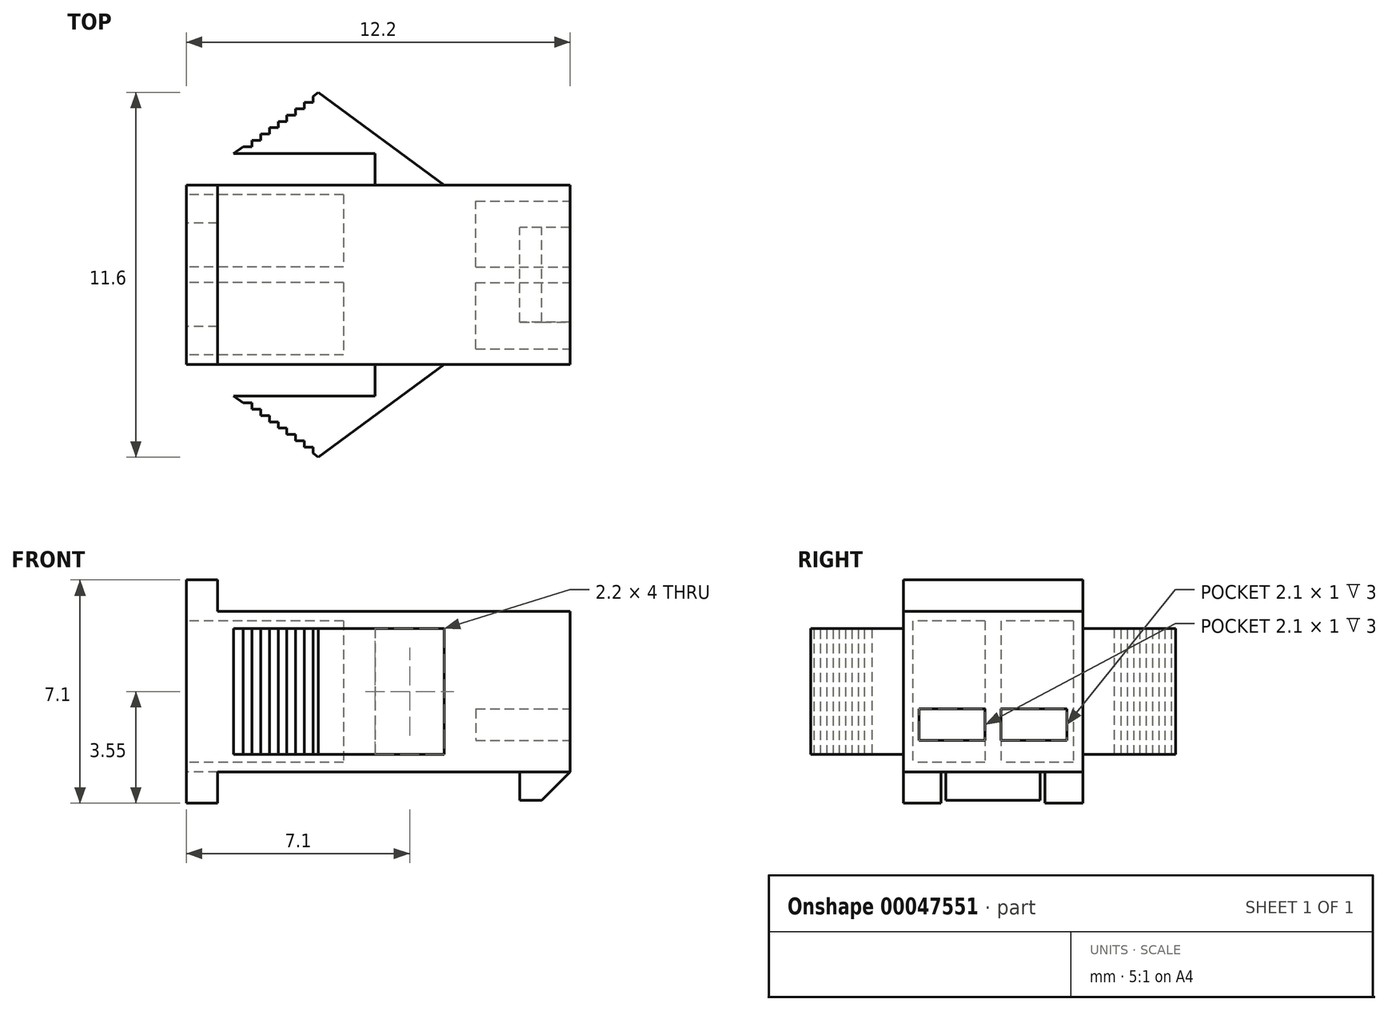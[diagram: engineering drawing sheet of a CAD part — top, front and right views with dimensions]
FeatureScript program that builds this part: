
annotation { "Feature Type Name" : "Feature", "Feature Type Description" : "" }
export const myFeature = defineFeature(function(context is Context, id is Id, definition is map)
    precondition{}
    {
        {
            var Q0;
            Q0=qCreatedBy(makeId("Top.planeOp"),FACE);
            var sketch = newSketch(context, id + "F0", { "sketchPlane" : qUnion([Q0])});
            skLineSegment(sketch, "E0.bottom", {"start": v(-6.1, 2.85) * mm, "end": v(-0.1, 2.85) * mm});
            skLineSegment(sketch, "E0.top", {"start": v(-6.1, -2.85) * mm, "end": v(-0.1, -2.85) * mm});
            skLineSegment(sketch, "E0.left", {"start": v(-6.1, 2.85) * mm, "end": v(-6.1, -2.85) * mm});
            skLineSegment(sketch, "E0.right", {"start": v(6.1, 2.85) * mm, "end": v(6.1, -2.85) * mm});
            skLineSegment(sketch, "E1", {"start": v(2.1, 2.85) * mm, "end": v(-1.9, 5.8) * mm});
            skLineSegment(sketch, "E2", {"start": v(2.1, -2.85) * mm, "end": v(-1.9, -5.8) * mm});
            skLineSegment(sketch, "E3", {"start": v(-4.6, 3.85) * mm, "end": v(-0.1, 3.85) * mm});
            skLineSegment(sketch, "E4", {"start": v(-1.9, 5.8) * mm, "end": v(-4.6, 3.85) * mm});
            skLineSegment(sketch, "E5.trimOffspring", {"start": v(-0.1, 3.85) * mm, "end": v(-0.1, 2.85) * mm});
            skLineSegment(sketch, "E6.trimOffspring", {"start": v(-0.1, -2.85) * mm, "end": v(-0.1, -3.85) * mm});
            skLineSegment(sketch, "E7", {"start": v(-4.6, -3.85) * mm, "end": v(-0.1, -3.85) * mm});
            skLineSegment(sketch, "E8", {"start": v(-4.6, -3.85) * mm, "end": v(-1.9, -5.8) * mm});
            skLineSegment(sketch, "E9.trimOffspring", {"start": v(2.1, 2.85) * mm, "end": v(6.1, 2.85) * mm});
            skLineSegment(sketch, "E10.trimOffspring", {"start": v(2.1, -2.85) * mm, "end": v(6.1, -2.85) * mm});
            skSolve(sketch);
        }
        {
            var Q0;
            Q0 = qSketchRegion(id + "F0", true);
            extrude(context, id + "F1", {"entities" : qUnion([Q0]), "depth" : 5.1 * mm});
        }
        {
            var Q0;
            Q0=makeQuery(id+"F1.opExtrude","SWEPT_FACE",FACE,{"disambiguationData":[OSD([sQuery(id+"F0.wireOp",EDGE,"E0.right")])]});
            var sketch = newSketch(context, id + "F2", { "sketchPlane" : qUnion([Q0])});
            skLineSegment(sketch, "E11", {"start": v(-6.2, 5.1) * mm, "end": v(-6.2, 4.55) * mm});
            skLineSegment(sketch, "E12", {"start": v(-6.2, 4.55) * mm, "end": v(-2.85, 4.55) * mm});
            skLineSegment(sketch, "E13", {"start": v(-6.2, 0.55) * mm, "end": v(-2.85, 0.55) * mm});
            skLineSegment(sketch, "E14", {"start": v(6.15, 5.1) * mm, "end": v(6.15, 4.55) * mm});
            skLineSegment(sketch, "E15", {"start": v(-2.85, 4.55) * mm, "end": v(-2.85, 5.1) * mm});
            skLineSegment(sketch, "E16", {"start": v(-2.85, 5.1) * mm, "end": v(-6.2, 5.1) * mm});
            skLineSegment(sketch, "E17", {"start": v(-2.85, 0.55) * mm, "end": v(-2.85, 0) * mm});
            skLineSegment(sketch, "E18", {"start": v(-2.85, 0) * mm, "end": v(-6.2, 0) * mm});
            skLineSegment(sketch, "E19", {"start": v(2.85, 4.55) * mm, "end": v(2.85, 5.1) * mm});
            skLineSegment(sketch, "E20", {"start": v(2.85, 5.1) * mm, "end": v(6.15, 5.1) * mm});
            skLineSegment(sketch, "E21", {"start": v(2.85, 0.55) * mm, "end": v(2.85, 0) * mm});
            skLineSegment(sketch, "E22", {"start": v(2.85, 0) * mm, "end": v(6.15, 0) * mm});
            skLineSegment(sketch, "E23.trimOffspring", {"start": v(6.15, 0.55) * mm, "end": v(6.15, 0) * mm});
            skLineSegment(sketch, "E24.trimOffspring", {"start": v(-6.2, 0.55) * mm, "end": v(-6.2, 0) * mm});
            skLineSegment(sketch, "E25.trimOffspring", {"start": v(2.85, 4.55) * mm, "end": v(6.15, 4.55) * mm});
            skLineSegment(sketch, "E26.trimOffspring", {"start": v(2.85, 0.55) * mm, "end": v(6.15, 0.55) * mm});
            skSolve(sketch);
        }
        {
            var Q0;
            Q0 = qSketchRegion(id + "F2", true);
            extrude(context, id + "F3", {"entities" : qUnion([Q0]), "operationType" : NewBodyOperationType.REMOVE, "oppositeDirection" : true, "depth" : 15 * mm});
        }
        {
            var Q0;
            Q0=makeQuery(id+"F3.boolean.opBoolean","COPY",FACE,{"derivedFrom":makeQuery(id+"F3.opExtrude","SWEPT_FACE",FACE,{"disambiguationData":[OSD([sQuery(id+"F2.wireOp",EDGE,"E25.trimOffspring")])]})});
            var sketch = newSketch(context, id + "F4", { "sketchPlane" : qUnion([Q0])});
            skLineSegment(sketch, "E27.0", {"start": v(-2.07, 5.48) * mm, "end": v(-2.35, 5.48) * mm});
            skLineSegment(sketch, "E28.0", {"start": v(-2.35, 5.28) * mm, "end": v(-2.63, 5.28) * mm});
            skLineSegment(sketch, "E29.0", {"start": v(-2.63, 5.08) * mm, "end": v(-2.9, 5.08) * mm});
            skLineSegment(sketch, "E30.0", {"start": v(-2.9, 4.88) * mm, "end": v(-3.18, 4.88) * mm});
            skLineSegment(sketch, "E31.0", {"start": v(-3.18, 4.68) * mm, "end": v(-3.46, 4.68) * mm});
            skLineSegment(sketch, "E32.0", {"start": v(-3.46, 4.48) * mm, "end": v(-3.73, 4.48) * mm});
            skLineSegment(sketch, "E33.0", {"start": v(-3.73, 4.28) * mm, "end": v(-4.01, 4.28) * mm});
            skLineSegment(sketch, "E34", {"start": v(-2.07, 5.68) * mm, "end": v(-2.07, 5.48) * mm});
            skLineSegment(sketch, "E35", {"start": v(-2.35, 5.48) * mm, "end": v(-2.35, 5.28) * mm});
            skLineSegment(sketch, "E36", {"start": v(-2.63, 5.28) * mm, "end": v(-2.63, 5.08) * mm});
            skLineSegment(sketch, "E37", {"start": v(-2.9, 5.08) * mm, "end": v(-2.9, 4.88) * mm});
            skLineSegment(sketch, "E38", {"start": v(-3.18, 4.88) * mm, "end": v(-3.18, 4.68) * mm});
            skLineSegment(sketch, "E39", {"start": v(-3.46, 4.68) * mm, "end": v(-3.46, 4.48) * mm});
            skLineSegment(sketch, "E40", {"start": v(-3.73, 4.48) * mm, "end": v(-3.73, 4.28) * mm});
            skLineSegment(sketch, "E41.0", {"start": v(-4.01, 4.08) * mm, "end": v(-4.29, 4.08) * mm});
            skLineSegment(sketch, "E42", {"start": v(-4.01, 4.28) * mm, "end": v(-4.01, 4.08) * mm});
            skLineSegment(sketch, "E43", {"start": v(-2.07, 5.68) * mm, "end": v(-4.29, 4.08) * mm});
            skLineSegment(sketch, "E44.MirrorCS", {"start": v(-3.46, -4.68) * mm, "end": v(-3.46, -4.48) * mm});
            skLineSegment(sketch, "E45.MirrorCS", {"start": v(-3.18, -4.88) * mm, "end": v(-3.18, -4.68) * mm});
            skLineSegment(sketch, "E46.MirrorCS", {"start": v(-3.18, -4.68) * mm, "end": v(-3.46, -4.68) * mm});
            skLineSegment(sketch, "E47.MirrorCS", {"start": v(-2.9, -5.08) * mm, "end": v(-2.9, -4.88) * mm});
            skLineSegment(sketch, "E48.MirrorCS", {"start": v(-2.63, -5.28) * mm, "end": v(-2.63, -5.08) * mm});
            skLineSegment(sketch, "E49.MirrorCS", {"start": v(-2.35, -5.48) * mm, "end": v(-2.35, -5.28) * mm});
            skLineSegment(sketch, "E50.MirrorCS", {"start": v(-2.07, -5.68) * mm, "end": v(-2.07, -5.48) * mm});
            skLineSegment(sketch, "E51.MirrorCS", {"start": v(-3.73, -4.28) * mm, "end": v(-4.01, -4.28) * mm});
            skLineSegment(sketch, "E52.MirrorCS", {"start": v(-3.46, -4.48) * mm, "end": v(-3.73, -4.48) * mm});
            skLineSegment(sketch, "E53.MirrorCS", {"start": v(-2.9, -4.88) * mm, "end": v(-3.18, -4.88) * mm});
            skLineSegment(sketch, "E54.MirrorCS", {"start": v(-2.63, -5.08) * mm, "end": v(-2.9, -5.08) * mm});
            skLineSegment(sketch, "E55.MirrorCS", {"start": v(-2.35, -5.28) * mm, "end": v(-2.63, -5.28) * mm});
            skLineSegment(sketch, "E56.MirrorCS", {"start": v(-2.07, -5.48) * mm, "end": v(-2.35, -5.48) * mm});
            skLineSegment(sketch, "E57.MirrorCS", {"start": v(-4.01, -4.28) * mm, "end": v(-4.01, -4.08) * mm});
            skLineSegment(sketch, "E58.MirrorCS", {"start": v(-4.01, -4.08) * mm, "end": v(-4.29, -4.08) * mm});
            skLineSegment(sketch, "E59.MirrorCS", {"start": v(-3.73, -4.48) * mm, "end": v(-3.73, -4.28) * mm});
            skLineSegment(sketch, "E60.MirrorCS", {"start": v(-2.07, -5.68) * mm, "end": v(-4.29, -4.08) * mm});
            skSolve(sketch);
        }
        {
            var Q0;
            Q0 = qSketchRegion(id + "F4", true);
            extrude(context, id + "F5", {"entities" : qUnion([Q0]), "operationType" : NewBodyOperationType.REMOVE, "oppositeDirection" : true, "depth" : 25 * mm});
        }
        {
            var Q0;
            Q0 = qSketchRegion(id + "F4", true);
            extrude(context, id + "F6", {"entities" : qUnion([Q0]), "operationType" : NewBodyOperationType.REMOVE, "oppositeDirection" : true, "depth" : 10 * mm});
        }
        {
            var Q0;
            Q0=makeQuery(id+"F1.opExtrude","SWEPT_FACE",FACE,{"disambiguationData":[OSD([sQuery(id+"F0.wireOp",EDGE,"E0.left")])]});
            var sketch = newSketch(context, id + "F7", { "sketchPlane" : qUnion([Q0])});
            skLineSegment(sketch, "E61", {"start": v(-2.85, 5.1) * mm, "end": v(-2.85, 6.1) * mm});
            skLineSegment(sketch, "E62", {"start": v(-2.85, 6.1) * mm, "end": v(2.85, 6.1) * mm});
            skLineSegment(sketch, "E63", {"start": v(2.85, 5.1) * mm, "end": v(2.85, 6.1) * mm});
            skPoint(sketch, "E63.endSnap0", {"position": v(0.35, 6.1) * mm});
            skLineSegment(sketch, "E64", {"start": v(-2.85, 5.1) * mm, "end": v(2.85, 5.1) * mm});
            skLineSegment(sketch, "E65", {"start": v(-2.85, 0) * mm, "end": v(-1.65, 0) * mm});
            skLineSegment(sketch, "E66", {"start": v(2.85, 0) * mm, "end": v(2.85, -1) * mm});
            skLineSegment(sketch, "E67", {"start": v(2.85, -1) * mm, "end": v(1.65, -1) * mm});
            skLineSegment(sketch, "E68", {"start": v(-2.85, -1) * mm, "end": v(-2.85, 0) * mm});
            skLineSegment(sketch, "E69", {"start": v(1.65, 0) * mm, "end": v(1.65, -1) * mm});
            skLineSegment(sketch, "E70", {"start": v(-1.65, 0) * mm, "end": v(-1.65, -1) * mm});
            skLineSegment(sketch, "E71.trimOffspring", {"start": v(-1.65, -1) * mm, "end": v(-2.85, -1) * mm});
            skLineSegment(sketch, "E72.trimOffspring", {"start": v(1.65, 0) * mm, "end": v(2.85, 0) * mm});
            skSolve(sketch);
        }
        {
            var Q0;
            Q0 = qSketchRegion(id + "F7", true);
            extrude(context, id + "F8", {"entities" : qUnion([Q0]), "oppositeDirection" : true, "depth" : 1 * mm});
        }
        {
            var Q0;
            Q0=makeQuery(id+"F1.opExtrude","SWEPT_BODY",BODY,{"disambiguationData":[OSD([sQuery(id+"F0.wireOp",EDGE,"E0.bottom"),sQuery(id+"F0.wireOp",EDGE,"E0.top"),sQuery(id+"F0.wireOp",EDGE,"E0.left"),sQuery(id+"F0.wireOp",EDGE,"E0.right"),sQuery(id+"F0.wireOp",EDGE,"E1"),sQuery(id+"F0.wireOp",EDGE,"E2"),sQuery(id+"F0.wireOp",EDGE,"E3"),sQuery(id+"F0.wireOp",EDGE,"E4"),sQuery(id+"F0.wireOp",EDGE,"E5.trimOffspring"),sQuery(id+"F0.wireOp",EDGE,"E6.trimOffspring"),sQuery(id+"F0.wireOp",EDGE,"E7"),sQuery(id+"F0.wireOp",EDGE,"E8"),sQuery(id+"F0.wireOp",EDGE,"E9.trimOffspring"),sQuery(id+"F0.wireOp",EDGE,"E10.trimOffspring")])]});
            var Q1;
            Q1=makeQuery(id+"F8.opExtrude","SWEPT_BODY",BODY,{"disambiguationData":[OSD([sQuery(id+"F7.wireOp",EDGE,"E65"),sQuery(id+"F7.wireOp",EDGE,"E68"),sQuery(id+"F7.wireOp",EDGE,"E70"),sQuery(id+"F7.wireOp",EDGE,"E71.trimOffspring")])]});
            var Q2;
            Q2=makeQuery(id+"F8.opExtrude","SWEPT_BODY",BODY,{"disambiguationData":[OSD([sQuery(id+"F7.wireOp",EDGE,"E66"),sQuery(id+"F7.wireOp",EDGE,"E67"),sQuery(id+"F7.wireOp",EDGE,"E69"),sQuery(id+"F7.wireOp",EDGE,"E72.trimOffspring")])]});
            var Q3;
            Q3=makeQuery(id+"F8.opExtrude","SWEPT_BODY",BODY,{"disambiguationData":[OSD([sQuery(id+"F7.wireOp",EDGE,"E61"),sQuery(id+"F7.wireOp",EDGE,"E62"),sQuery(id+"F7.wireOp",EDGE,"E63"),sQuery(id+"F7.wireOp",EDGE,"E64")])]});
            booleanBodies(context, id + "F9", {"operationType" : BooleanOperationType.UNION, "tools" : qUnion([Q0, Q1, Q2, Q3])});
        }
        {
            var Q0;
            Q0=makeQuery(id+"F9.opBoolean","MERGE",FACE,{"derivedFrom":[makeQuery(id+"F3.boolean.opBoolean","MERGE",FACE,{"derivedFrom":[makeQuery(id+"F1.opExtrude","SWEPT_FACE",FACE,{"disambiguationData":[OSD([sQuery(id+"F0.wireOp",EDGE,"E0.bottom")])]}),makeQuery(id+"F1.opExtrude","SWEPT_FACE",FACE,{"disambiguationData":[OSD([sQuery(id+"F0.wireOp",EDGE,"E9.trimOffspring")])]}),makeQuery(id+"F3.opExtrude","SWEPT_FACE",FACE,{"disambiguationData":[OSD([sQuery(id+"F2.wireOp",EDGE,"E19")])]}),makeQuery(id+"F3.opExtrude","SWEPT_FACE",FACE,{"disambiguationData":[OSD([sQuery(id+"F2.wireOp",EDGE,"E21")])]})]}),makeQuery(id+"F8.opExtrude","SWEPT_FACE",FACE,{"disambiguationData":[OSD([sQuery(id+"F7.wireOp",EDGE,"E61")])]}),makeQuery(id+"F8.opExtrude","SWEPT_FACE",FACE,{"disambiguationData":[OSD([sQuery(id+"F7.wireOp",EDGE,"E68")])]})]});
            var sketch = newSketch(context, id + "F10", { "sketchPlane" : qUnion([Q0])});
            skLineSegment(sketch, "E73", {"start": v(-5.2, -0.9) * mm, "end": v(-4.5, -0.9) * mm});
            skLineSegment(sketch, "E74", {"start": v(-4.5, -0.9) * mm, "end": v(-4.5, 0) * mm});
            skLineSegment(sketch, "E75", {"start": v(-6.1, 0) * mm, "end": v(-5.2, -0.9) * mm});
            skLineSegment(sketch, "E76", {"start": v(-4.5, 0) * mm, "end": v(-6.1, 0) * mm});
            skSolve(sketch);
        }
        {
            var Q0;
            Q0 = qSketchRegion(id + "F10", true);
            var Q1;
            Q1=makeQuery(id+"F9.opBoolean","MERGE",FACE,{"derivedFrom":[makeQuery(id+"F3.boolean.opBoolean","MERGE",FACE,{"derivedFrom":[makeQuery(id+"F1.opExtrude","SWEPT_FACE",FACE,{"disambiguationData":[OSD([sQuery(id+"F0.wireOp",EDGE,"E0.top")])]}),makeQuery(id+"F1.opExtrude","SWEPT_FACE",FACE,{"disambiguationData":[OSD([sQuery(id+"F0.wireOp",EDGE,"E10.trimOffspring")])]}),makeQuery(id+"F3.opExtrude","SWEPT_FACE",FACE,{"disambiguationData":[OSD([sQuery(id+"F2.wireOp",EDGE,"E15")])]}),makeQuery(id+"F3.opExtrude","SWEPT_FACE",FACE,{"disambiguationData":[OSD([sQuery(id+"F2.wireOp",EDGE,"E17")])]})]}),makeQuery(id+"F8.opExtrude","SWEPT_FACE",FACE,{"disambiguationData":[OSD([sQuery(id+"F7.wireOp",EDGE,"E63")])]}),makeQuery(id+"F8.opExtrude","SWEPT_FACE",FACE,{"disambiguationData":[OSD([sQuery(id+"F7.wireOp",EDGE,"E66")])]})]});
            extrude(context, id + "F11", {"entities" : qUnion([Q0]), "operationType" : NewBodyOperationType.ADD, "endBound" : BoundingType.UP_TO_SURFACE, "oppositeDirection" : true, "endBoundEntityFace" : qUnion([Q1]), "depth" : 25 * mm});
        }
        {
            var Q0;
            Q0=makeQuery(id+"F11.opExtrude","SWEPT_FACE",FACE,{"disambiguationData":[OSD([sQuery(id+"F10.wireOp",EDGE,"E74")])]});
            var sketch = newSketch(context, id + "F12", { "sketchPlane" : qUnion([Q0])});
            skLineSegment(sketch, "E77", {"start": v(1.5, 0) * mm, "end": v(1.5, -1.4) * mm});
            skLineSegment(sketch, "E78", {"start": v(-1.5, -1.43) * mm, "end": v(-1.5, 0) * mm});
            skLineSegment(sketch, "E79", {"start": v(-1.5, 0) * mm, "end": v(-3.12, 0) * mm});
            skLineSegment(sketch, "E80", {"start": v(-3.12, 0) * mm, "end": v(-3.12, -1.43) * mm});
            skLineSegment(sketch, "E81", {"start": v(-1.5, -1.43) * mm, "end": v(-3.12, -1.43) * mm});
            skLineSegment(sketch, "E82", {"start": v(1.5, 0) * mm, "end": v(3.09, 0) * mm});
            skLineSegment(sketch, "E83", {"start": v(3.09, 0) * mm, "end": v(3.09, -1.4) * mm});
            skLineSegment(sketch, "E84", {"start": v(3.09, -1.4) * mm, "end": v(1.5, -1.4) * mm});
            skSolve(sketch);
        }
        {
            var Q0;
            Q0 = qSketchRegion(id + "F12", true);
            extrude(context, id + "F13", {"entities" : qUnion([Q0]), "operationType" : NewBodyOperationType.REMOVE, "oppositeDirection" : true, "depth" : 3 * mm});
        }
        {
            var Q0;
            Q0=makeQuery(id+"F1.opExtrude","SWEPT_FACE",FACE,{"disambiguationData":[OSD([sQuery(id+"F0.wireOp",EDGE,"E0.right")])]});
            var sketch = newSketch(context, id + "F14", { "sketchPlane" : qUnion([Q0])});
            skLineSegment(sketch, "E85.bottom", {"start": v(-2.35, 2) * mm, "end": v(-0.25, 2) * mm});
            skLineSegment(sketch, "E85.top", {"start": v(-2.35, 1) * mm, "end": v(-0.25, 1) * mm});
            skLineSegment(sketch, "E86", {"start": v(-2.35, 2) * mm, "end": v(-2.35, 1) * mm});
            skLineSegment(sketch, "E87", {"start": v(2.35, 2) * mm, "end": v(2.35, 1) * mm});
            skLineSegment(sketch, "E88", {"start": v(0.25, 2) * mm, "end": v(0.25, 1) * mm});
            skLineSegment(sketch, "E89", {"start": v(-0.25, 2) * mm, "end": v(-0.25, 1) * mm});
            skLineSegment(sketch, "E90.trimOffspring", {"start": v(0.25, 2) * mm, "end": v(2.35, 2) * mm});
            skLineSegment(sketch, "E91.trimOffspring", {"start": v(0.25, 1) * mm, "end": v(2.35, 1) * mm});
            skSolve(sketch);
        }
        {
            var Q0;
            Q0 = qSketchRegion(id + "F14", true);
            extrude(context, id + "F15", {"entities" : qUnion([Q0]), "operationType" : NewBodyOperationType.REMOVE, "oppositeDirection" : true, "depth" : 3 * mm});
        }
        {
            var Q0;
            Q0=makeQuery(id+"F9.opBoolean","MERGE",FACE,{"derivedFrom":[makeQuery(id+"F1.opExtrude","SWEPT_FACE",FACE,{"disambiguationData":[OSD([sQuery(id+"F0.wireOp",EDGE,"E0.left")])]}),makeQuery(id+"F8.opExtrude","CAP_FACE",FACE,{"disambiguationData":[OSD([sQuery(id+"F7.wireOp",EDGE,"E61"),sQuery(id+"F7.wireOp",EDGE,"E62"),sQuery(id+"F7.wireOp",EDGE,"E63"),sQuery(id+"F7.wireOp",EDGE,"E64")])],"isStart":true}),makeQuery(id+"F8.opExtrude","CAP_FACE",FACE,{"disambiguationData":[OSD([sQuery(id+"F7.wireOp",EDGE,"E65"),sQuery(id+"F7.wireOp",EDGE,"E68"),sQuery(id+"F7.wireOp",EDGE,"E70"),sQuery(id+"F7.wireOp",EDGE,"E71.trimOffspring")])],"isStart":true}),makeQuery(id+"F8.opExtrude","CAP_FACE",FACE,{"disambiguationData":[OSD([sQuery(id+"F7.wireOp",EDGE,"E66"),sQuery(id+"F7.wireOp",EDGE,"E67"),sQuery(id+"F7.wireOp",EDGE,"E69"),sQuery(id+"F7.wireOp",EDGE,"E72.trimOffspring")])],"isStart":true})]});
            var sketch = newSketch(context, id + "F16", { "sketchPlane" : qUnion([Q0])});
            skLineSegment(sketch, "E92.bottom", {"start": v(-2.55, 4.8) * mm, "end": v(-0.25, 4.8) * mm});
            skLineSegment(sketch, "E92.top", {"start": v(-2.55, 0.3) * mm, "end": v(-0.25, 0.3) * mm});
            skLineSegment(sketch, "E92.left", {"start": v(-2.55, 4.8) * mm, "end": v(-2.55, 0.3) * mm});
            skLineSegment(sketch, "E92.right", {"start": v(2.55, 4.8) * mm, "end": v(2.55, 0.3) * mm});
            skLineSegment(sketch, "E93", {"start": v(-0.25, 4.8) * mm, "end": v(-0.25, 0.3) * mm});
            skLineSegment(sketch, "E94", {"start": v(0.25, 4.8) * mm, "end": v(0.25, 0.3) * mm});
            skLineSegment(sketch, "E95.trimOffspring", {"start": v(0.25, 4.8) * mm, "end": v(2.55, 4.8) * mm});
            skLineSegment(sketch, "E96.trimOffspring", {"start": v(0.25, 0.3) * mm, "end": v(2.55, 0.3) * mm});
            skSolve(sketch);
        }
        {
            var Q0;
            Q0 = qSketchRegion(id + "F16", true);
            extrude(context, id + "F17", {"entities" : qUnion([Q0]), "operationType" : NewBodyOperationType.REMOVE, "oppositeDirection" : true, "depth" : 5 * mm});
        }
    });
